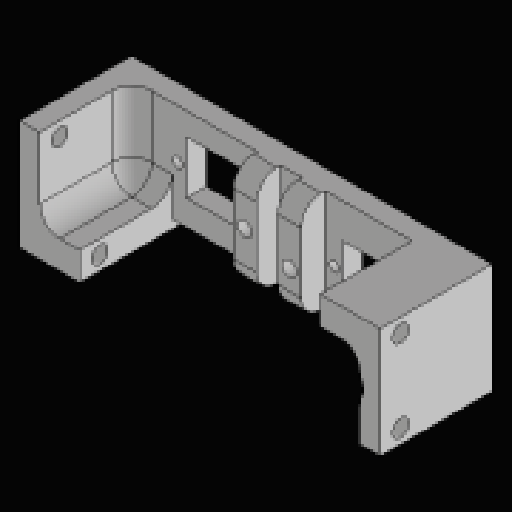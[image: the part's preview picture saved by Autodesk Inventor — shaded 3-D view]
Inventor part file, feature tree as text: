
AUTODESK INVENTOR PART (.ipt)
format: ipt  version: 2023.2 (Build 272271030, 271C)  size: 587,776 bytes
history: native  units: mm
features: sketch x8, projected_geometry x7, reference x6, extrude x5, other x5, hole x2, fillet x1
ambient origin geometry x8: Origin, YZ Plane, XZ Plane, XY Plane, X Axis, Y Axis, Z Axis, Center Point
bodies: Solid1 (feature_tree)
feature tree (34):
  extrude  "Extrusion1"  Depth=7.0mm
  hole  "Hole1"  [1 undecoded]
  extrude  "Extrusion2"  Depth=10.0mm TaperAngle=0.0deg
  extrude  "Extrusion3"  Depth=5.0mm
  extrude  "Extrusion4"  Depth=0.5mm
  hole  "Hole2"  [1 undecoded]
  extrude  "Extrusion5"  Depth=5.0mm
  fillet  "Fillet1"  Radius=5.8mm
  sketch  "Sketch8"  dims[d21=5.0mm d22=0.0mm d23=5.8mm d24=5.8mm d25=6.0mm d26=0.0mm d27=2.5mm d28=6.0mm d29=3.7mm d30=3.5mm d31=90.0deg d32=8.0mm d33=20.594885mm d34=5.0mm d35=0.0mm d36=0.0mm d37=5.0mm d38=5.65mm d39=13.2mm d40=8.65mm d41=23.5mm d42=18.658804mm d43=8.741196mm d44=5.65mm d45=5.0mm d46=15.0mm d47=7.0mm d48=27.8mm d49=11.1mm d50=39.258804mm d51=39.641196mm]
  sketch  "Sketch1"  dims[d0=27.5mm d1=7.0mm]
  sketch  "Sketch2"  dims[d2=10.0mm d3=5.0mm]
  projected_geometry  "Projected Loop1"
  sketch  "Sketch3"  dims[d4=70.0mm d5=10.0mm d6=0.0mm]
  projected_geometry  "Projected Loop2"
  projected_geometry  "Projected Loop3"
  sketch  "Sketch4"  dims[d7=20.45mm]
  projected_geometry  "Projected Loop4"
  projected_geometry  "Projected Loop5"
  reference  "Reference1"
  reference  "Reference2"
  reference  "Reference3"
  reference  "Reference4"
  sketch  "Sketch5"  dims[d8=4.2mm d9=6.0mm d10=4.5mm d11=2.5mm d12=90.0deg d13=8.0mm d14=20.594885mm d15=5.0mm]
  reference  "Reference5"
  reference  "Reference6"
  projected_geometry  "Projected Loop6"
  sketch  "Sketch6"  dims[d16=17.95mm d17=0.0mm d18=0.5mm]
  sketch  "Sketch7"  dims[d19=0.5mm d20=2.5mm]
  projected_geometry  "Projected Loop7"
  other  "Horizontal Leg Test v3.iam"
  other  "SG90 - Micro Servo 9g - Tower Pro:2"
  other  "SG90 - Micro Servo 9g - Tower Pro:1"
  other  "Intermediate Gear:2"
  other  "Intermediate Gear:1"
note: 2 required parameter values undecoded (feature->parameter linkage not recoverable at this tier; creation-order binding heuristic only, values carry confidence <= 0.55)
